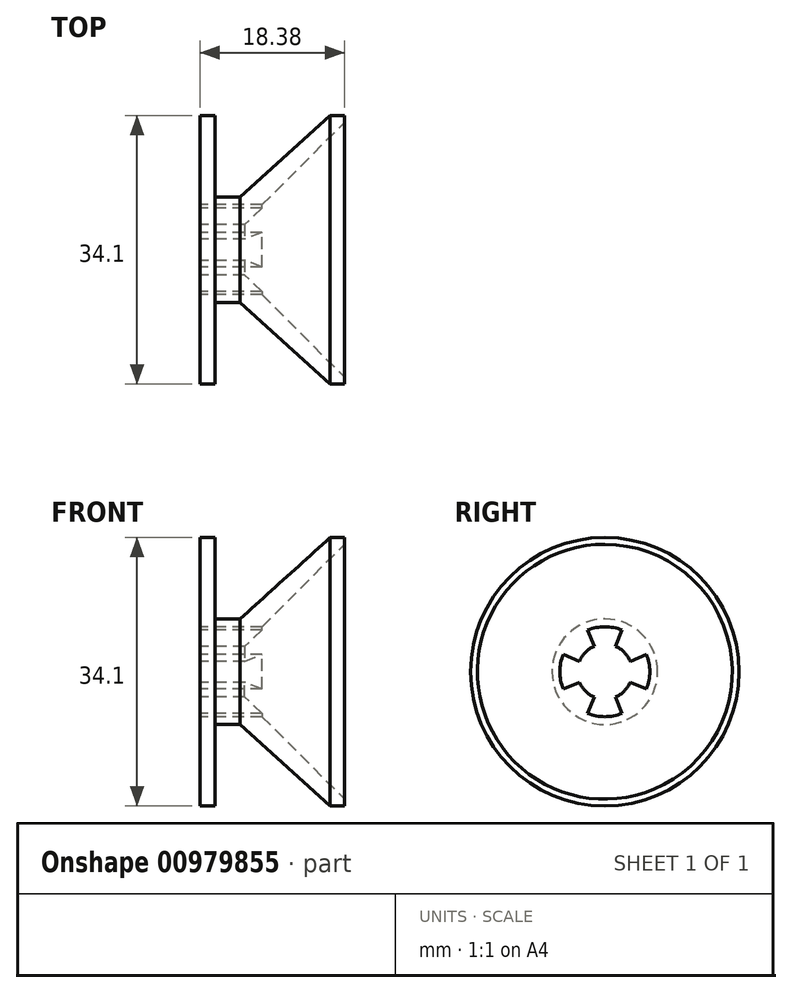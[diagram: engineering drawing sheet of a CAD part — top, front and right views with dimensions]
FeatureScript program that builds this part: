
annotation { "Feature Type Name" : "Feature", "Feature Type Description" : "" }
export const myFeature = defineFeature(function(context is Context, id is Id, definition is map)
    precondition{}
    {
        {
            var Q0;
            Q0=qCreatedBy(makeId("Front.planeOp"),FACE);
            var sketch = newSketch(context, id + "F0", { "sketchPlane" : qUnion([Q0])});
            skPoint(sketch, "E0", {"position": v(16.68, 17.05) * mm});
            skLineSegment(sketch, "E1", {"start": v(0, 0) * mm, "end": v(7.84, 0) * mm});
            skLineSegment(sketch, "E2", {"start": v(2.04, 6.7) * mm, "end": v(5.21, 6.7) * mm});
            skLineSegment(sketch, "E3", {"start": v(16.68, 17.05) * mm, "end": v(5.21, 6.7) * mm});
            skPoint(sketch, "E4.visualSharp", {"position": v(2.04, 17.05) * mm});
            skLineSegment(sketch, "E5", {"start": v(2.04, 6.7) * mm, "end": v(2.04, 17.05) * mm});
            skLineSegment(sketch, "E6", {"start": v(0.13, 17.05) * mm, "end": v(2.04, 17.05) * mm});
            skLineSegment(sketch, "E7", {"start": v(18.51, 16.19) * mm, "end": v(18.51, 17.05) * mm});
            skLineSegment(sketch, "E8", {"start": v(18.51, 17.05) * mm, "end": v(16.68, 17.05) * mm});
            skLineSegment(sketch, "E9", {"start": v(0.13, 3.5) * mm, "end": v(5.82, 3.5) * mm});
            skLineSegment(sketch, "E10", {"start": v(5.82, 3.5) * mm, "end": v(18.51, 16.19) * mm});
            skLineSegment(sketch, "E11", {"start": v(0.13, 17.05) * mm, "end": v(0.13, 3.5) * mm});
            skSolve(sketch);
        }
        {
            var Q0;
            Q0=makeQuery(id+"F0.imprint","IMPRINT",FACE,{"disambiguationData":[TD([[makeQuery(id+"F0.imprint","IMPRINT",EDGE,{"derivedFrom":sQuery(id+"F0.wireOp",EDGE,"E2")}),-1.0]])]});
            var Q1;
            Q1=sQuery(id+"F0.wireOp",EDGE,"E1");
            revolve(context, id + "F1", {"entities" : qUnion([Q0]), "axis" : qUnion([Q1]), "revolveType" : RevolveType.FULL});
        }
        {
            var Q0;
            Q0=makeQuery(id+"F1.opRevolve","SWEPT_FACE",FACE,{"disambiguationData":[OSD([sQuery(id+"F0.wireOp",EDGE,"E11")])]});
            var sketch = newSketch(context, id + "F2", { "sketchPlane" : qUnion([Q0])});
            skArc(sketch, "E12", {"start": v(3.23, -1.34) * mm, "mid": v(3.5, 0) * mm, "end": v(3.23, 1.34) * mm});
            skArc(sketch, "E13", {"start": v(-1.34, -3.23) * mm, "mid": v(0, -3.5) * mm, "end": v(1.34, -3.23) * mm});
            skArc(sketch, "E14", {"start": v(-3.23, 1.34) * mm, "mid": v(-3.5, 0) * mm, "end": v(-3.23, -1.34) * mm});
            skArc(sketch, "E15", {"start": v(1.34, 3.23) * mm, "mid": v(0, 3.5) * mm, "end": v(-1.34, 3.23) * mm});
            skLineSegment(sketch, "E16", {"start": v(-5.28, 2.19) * mm, "end": v(-3.23, 1.34) * mm});
            skLineSegment(sketch, "E17", {"start": v(-1.34, 3.23) * mm, "end": v(-2.19, 5.28) * mm});
            skLineSegment(sketch, "E18", {"start": v(2.19, 5.28) * mm, "end": v(1.34, 3.23) * mm});
            skLineSegment(sketch, "E19", {"start": v(3.23, 1.34) * mm, "end": v(5.28, 2.19) * mm});
            skLineSegment(sketch, "E20", {"start": v(3.23, -1.34) * mm, "end": v(5.28, -2.19) * mm});
            skLineSegment(sketch, "E21", {"start": v(1.34, -3.23) * mm, "end": v(2.19, -5.28) * mm});
            skLineSegment(sketch, "E22", {"start": v(-1.34, -3.23) * mm, "end": v(-2.19, -5.28) * mm});
            skLineSegment(sketch, "E23", {"start": v(-3.23, -1.34) * mm, "end": v(-5.28, -2.19) * mm});
            skArc(sketch, "E24", {"start": v(-5.28, 2.19) * mm, "mid": v(-5.72, 0) * mm, "end": v(-5.28, -2.19) * mm});
            skArc(sketch, "E25", {"start": v(-2.19, -5.28) * mm, "mid": v(0, -5.72) * mm, "end": v(2.19, -5.28) * mm});
            skArc(sketch, "E26", {"start": v(5.28, -2.19) * mm, "mid": v(5.72, 0) * mm, "end": v(5.28, 2.19) * mm});
            skArc(sketch, "E27", {"start": v(2.19, 5.28) * mm, "mid": v(0, 5.72) * mm, "end": v(-2.19, 5.28) * mm});
            skSolve(sketch);
        }
        {
            var Q0;
            Q0=qSketchRegion(id+"F2",true);
            extrude(context, id + "F3", {"entities" : qUnion([Q0]), "operationType" : NewBodyOperationType.REMOVE, "endBound" : BoundingType.UP_TO_NEXT, "oppositeDirection" : true, "depth" : 25.4 * mm});
        }
    });
